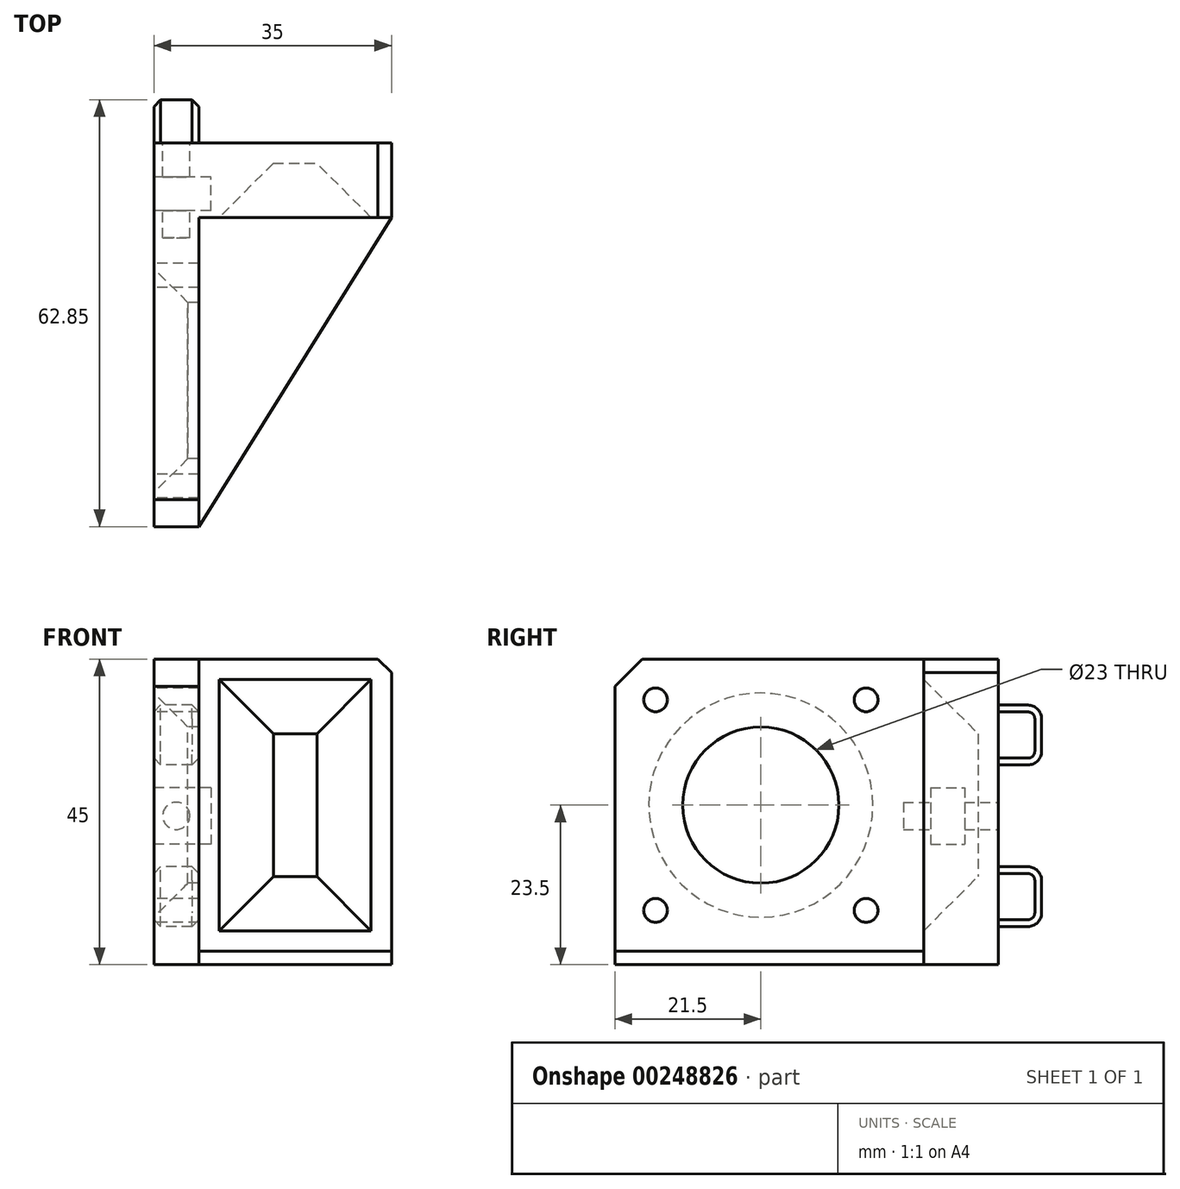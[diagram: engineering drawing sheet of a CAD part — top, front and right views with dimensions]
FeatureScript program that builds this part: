
annotation { "Feature Type Name" : "Feature", "Feature Type Description" : "" }
export const myFeature = defineFeature(function(context is Context, id is Id, definition is map)
    precondition{}
    {
        {
            var Q0;
            Q0=qCreatedBy(makeId("Right.planeOp"),FACE);
            var sketch = newSketch(context, id + "F0", { "sketchPlane" : qUnion([Q0])});
            skCircle(sketch, "E0", {"center": v(0, 0) * mm, "radius": 11.5 * mm});
            skCircle(sketch, "E1", {"center": v(15.5, 15.5) * mm, "radius": 1.75 * mm});
            skCircle(sketch, "E2.MirrorC", {"center": v(-15.5, 15.5) * mm, "radius": 1.75 * mm});
            skCircle(sketch, "E3.MirrorC", {"center": v(-15.5, -15.5) * mm, "radius": 1.75 * mm});
            skCircle(sketch, "E4.MirrorC", {"center": v(15.5, -15.5) * mm, "radius": 1.75 * mm});
            skLineSegment(sketch, "E5", {"start": v(-21.5, 21.5) * mm, "end": v(-21.5, -23.5) * mm});
            skPoint(sketch, "E6", {"position": v(-21.5, -1) * mm});
            skLineSegment(sketch, "E7", {"start": v(-21.5, 21.5) * mm, "end": v(35, 21.5) * mm});
            skLineSegment(sketch, "E8", {"start": v(35, 21.5) * mm, "end": v(35, -23.5) * mm});
            skLineSegment(sketch, "E9", {"start": v(35, -23.5) * mm, "end": v(-21.5, -23.5) * mm});
            skLineSegment(sketch, "E10", {"start": v(24, 21.5) * mm, "end": v(24, -23.5) * mm});
            skLineSegment(sketch, "E11", {"start": v(35, 14.72) * mm, "end": v(41.35, 14.72) * mm});
            skLineSegment(sketch, "E12", {"start": v(41.35, 14.72) * mm, "end": v(41.35, 5.92) * mm});
            skLineSegment(sketch, "E13", {"start": v(41.35, 5.92) * mm, "end": v(35, 5.92) * mm});
            skLineSegment(sketch, "E14", {"start": v(35, -9.08) * mm, "end": v(41.35, -9.08) * mm});
            skLineSegment(sketch, "E15", {"start": v(41.35, -9.08) * mm, "end": v(41.35, -17.88) * mm});
            skLineSegment(sketch, "E16", {"start": v(41.35, -17.88) * mm, "end": v(35, -17.88) * mm});
            skLineSegment(sketch, "E17", {"start": v(-21.5, -21.5) * mm, "end": v(24, -21.5) * mm});
            skSolve(sketch);
        }
        {
            var Q0;
            {var subQ6=sQuery(id+"F0.wireOp",EDGE,"E10");Q0=makeQuery(id+"F0.imprint","IMPRINT",FACE,{"disambiguationData":[TD([[makeQuery(id+"F0.imprint","IMPRINT",EDGE,{"derivedFrom":subQ6}),1.0]])]});}
            var Q1;
            {var subQ3=sQuery(id+"F0.wireOp",EDGE,"E17");Q1=makeQuery(id+"F0.imprint","IMPRINT",FACE,{"disambiguationData":[TD([[makeQuery(id+"F0.imprint","IMPRINT",EDGE,{"derivedFrom":subQ3}),-1.0]])]});}
            extrude(context, id + "F1", {"entities" : qUnion([Q0, Q1]), "depth" : 35 * mm, "offsetDistance" : 25 * mm});
        }
        {
            var Q0;
            Q0=makeQuery(id+"F0.imprint","IMPRINT",FACE,{"disambiguationData":[TD([[makeQuery(id+"F0.imprint","IMPRINT",EDGE,{"derivedFrom":sQuery(id+"F0.wireOp",EDGE,"E0")}),-1.0]])]});
            extrude(context, id + "F2", {"entities" : qUnion([Q0]), "operationType" : NewBodyOperationType.ADD, "depth" : 6.6 * mm, "offsetDistance" : 25 * mm});
        }
        {
            var Q0;
            {var subQ0=sQuery(id+"F0.wireOp",EDGE,"E11");Q0=makeQuery(id+"F0.imprint","IMPRINT",FACE,{"disambiguationData":[TD([[makeQuery(id+"F0.imprint","IMPRINT",EDGE,{"derivedFrom":subQ0}),-1.0]])]});}
            var Q1;
            {var subQ0=sQuery(id+"F0.wireOp",EDGE,"E14");Q1=makeQuery(id+"F0.imprint","IMPRINT",FACE,{"disambiguationData":[TD([[makeQuery(id+"F0.imprint","IMPRINT",EDGE,{"derivedFrom":subQ0}),-1.0]])]});}
            extrude(context, id + "F3", {"entities" : qUnion([Q0, Q1]), "operationType" : NewBodyOperationType.ADD, "depth" : 6.6 * mm, "offsetDistance" : 25 * mm});
        }
        {
            var Q0;
            Q0=makeQuery(id+"F1.opExtrude","SWEPT_FACE",FACE,{"disambiguationData":[OSD([sQuery(id+"F0.wireOp",EDGE,"E8")])]});
            var sketch = newSketch(context, id + "F4", { "sketchPlane" : qUnion([Q0])});
            skLineSegment(sketch, "E18", {"start": v(0, 5.92) * mm, "end": v(0, -9.08) * mm});
            skPoint(sketch, "E19", {"position": v(0, -1.58) * mm});
            skPoint(sketch, "E20", {"position": v(-3.3, -1.58) * mm});
            skPoint(sketch, "E20.positionSnap0", {"position": v(-3.3, -9.08) * mm});
            skCircle(sketch, "E21", {"center": v(-3.3, -1.58) * mm, "radius": 2 * mm});
            skSolve(sketch);
        }
        {
            var Q0;
            Q0=makeQuery(id+"F4.imprint","IMPRINT",FACE,{"disambiguationData":[TD([[makeQuery(id+"F4.imprint","IMPRINT",EDGE,{"derivedFrom":sQuery(id+"F4.wireOp",EDGE,"E21")}),1.0]])]});
            extrude(context, id + "F5", {"entities" : qUnion([Q0]), "operationType" : NewBodyOperationType.REMOVE, "oppositeDirection" : true, "depth" : 14 * mm, "offsetDistance" : 25 * mm});
        }
        {
            var Q0;
            {var subQ0=sQuery(id+"F0.wireOp",EDGE,"E8");var subQ1=sQuery(id+"F0.wireOp",EDGE,"E10");var subQ2=sQuery(id+"F0.wireOp",EDGE,"E9");var subQ3=sQuery(id+"F0.wireOp",EDGE,"E7");Q0=makeQuery(id+"F3.boolean.opBoolean","MERGE",FACE,{"derivedFrom":[makeQuery(id+"F2.boolean.opBoolean","MERGE",FACE,{"derivedFrom":[makeQuery(id+"F1.opExtrude","CAP_FACE",FACE,{"disambiguationData":[OSD([subQ3,subQ0,subQ2,subQ1])],"isStart":true}),makeQuery(id+"F2.opExtrude","CAP_FACE",FACE,{"disambiguationData":[OSD([sQuery(id+"F0.wireOp",EDGE,"E0"),sQuery(id+"F0.wireOp",EDGE,"E1"),sQuery(id+"F0.wireOp",EDGE,"E2.MirrorC"),sQuery(id+"F0.wireOp",EDGE,"E3.MirrorC"),sQuery(id+"F0.wireOp",EDGE,"E4.MirrorC"),sQuery(id+"F0.wireOp",EDGE,"E5"),subQ3,subQ2,subQ1])],"isStart":true})]}),makeQuery(id+"F3.opExtrude","CAP_FACE",FACE,{"disambiguationData":[OSD([subQ0,sQuery(id+"F0.wireOp",EDGE,"E11"),sQuery(id+"F0.wireOp",EDGE,"E12"),sQuery(id+"F0.wireOp",EDGE,"E13")])],"isStart":true}),makeQuery(id+"F3.opExtrude","CAP_FACE",FACE,{"disambiguationData":[OSD([subQ0,sQuery(id+"F0.wireOp",EDGE,"E14"),sQuery(id+"F0.wireOp",EDGE,"E15"),sQuery(id+"F0.wireOp",EDGE,"E16")])],"isStart":true})]});}
            var sketch = newSketch(context, id + "F6", { "sketchPlane" : qUnion([Q0])});
            skLineSegment(sketch, "E22.bottom", {"start": v(-25, 2.57) * mm, "end": v(-30, 2.57) * mm});
            skLineSegment(sketch, "E22.top", {"start": v(-25, -5.73) * mm, "end": v(-30, -5.73) * mm});
            skLineSegment(sketch, "E22.left", {"start": v(-25, 2.57) * mm, "end": v(-25, -5.73) * mm});
            skLineSegment(sketch, "E22.right", {"start": v(-30, 2.57) * mm, "end": v(-30, -5.73) * mm});
            skPoint(sketch, "E22.middle", {"position": v(-27.5, -1.58) * mm});
            skPoint(sketch, "E22.middle.positionSnap0", {"position": v(-35, -1.58) * mm});
            skPoint(sketch, "E22.centerSnap0", {"position": v(-35, -1.58) * mm});
            skSolve(sketch);
        }
        {
            var Q0;
            Q0=makeQuery(id+"F6.imprint","IMPRINT",FACE,{"disambiguationData":[TD([[makeQuery(id+"F6.imprint","IMPRINT",EDGE,{"derivedFrom":sQuery(id+"F6.wireOp",EDGE,"E22.bottom")}),1.0]])]});
            extrude(context, id + "F7", {"entities" : qUnion([Q0]), "operationType" : NewBodyOperationType.REMOVE, "oppositeDirection" : true, "depth" : (0.3 + 3.3 + 9.58 / 2) * mm, "offsetDistance" : 25 * mm});
        }
        {
            var Q0;
            Q0=makeQuery(id+"F1.opExtrude","CAP_EDGE",EDGE,{"disambiguationData":[OSD([sQuery(id+"F0.wireOp",EDGE,"E5")])],"isStart":false});
            chamfer(context, id + "F8", {"entities" : qUnion([Q0]), "chamferType" : ChamferType.TWO_OFFSETS, "width1" : 45.5 * mm, "oppositeDirection" : false, "width2" : 28.4 * mm, "tangentPropagation" : true});
        }
        {
            var Q0;
            Q0=makeQuery(id+"F3.opExtrude","SWEPT_EDGE",EDGE,{"disambiguationData":[OSD([sQuery(id+"F0.wireOp",EDGE,"E11"),sQuery(id+"F0.wireOp",EDGE,"E12")])]});
            var Q1;
            Q1=makeQuery(id+"F3.opExtrude","SWEPT_EDGE",EDGE,{"disambiguationData":[OSD([sQuery(id+"F0.wireOp",EDGE,"E12"),sQuery(id+"F0.wireOp",EDGE,"E13")])]});
            var Q2;
            Q2=makeQuery(id+"F3.opExtrude","SWEPT_EDGE",EDGE,{"disambiguationData":[OSD([sQuery(id+"F0.wireOp",EDGE,"E14"),sQuery(id+"F0.wireOp",EDGE,"E15")])]});
            var Q3;
            Q3=makeQuery(id+"F3.opExtrude","SWEPT_EDGE",EDGE,{"disambiguationData":[OSD([sQuery(id+"F0.wireOp",EDGE,"E15"),sQuery(id+"F0.wireOp",EDGE,"E16")])]});
            fillet(context, id + "F9", {"entities" : qUnion([Q0, Q1, Q2, Q3]), "radius" : 2 * mm, "tangentPropagation" : true, "allowEdgeOverflow" : false});
        }
        {
            var Q0;
            Q0=makeQuery(id+"F3.opExtrude","CAP_EDGE",EDGE,{"disambiguationData":[OSD([sQuery(id+"F0.wireOp",EDGE,"E14")])],"isStart":true});
            var Q1;
            Q1=makeQuery(id+"F3.opExtrude","CAP_EDGE",EDGE,{"disambiguationData":[OSD([sQuery(id+"F0.wireOp",EDGE,"E11")])],"isStart":true});
            var Q2;
            Q2=makeQuery(id+"F3.opExtrude","CAP_EDGE",EDGE,{"disambiguationData":[OSD([sQuery(id+"F0.wireOp",EDGE,"E16")])],"isStart":false});
            var Q3;
            Q3=makeQuery(id+"F3.opExtrude","CAP_EDGE",EDGE,{"disambiguationData":[OSD([sQuery(id+"F0.wireOp",EDGE,"E13")])],"isStart":false});
            chamfer(context, id + "F10", {"entities" : qUnion([Q0, Q1, Q2, Q3]), "width" : 1 * mm, "tangentPropagation" : true});
        }
        {
            var Q0;
            Q0=makeQuery(id+"F2.opExtrude","SWEPT_EDGE",EDGE,{"disambiguationData":[OSD([sQuery(id+"F0.wireOp",EDGE,"E5"),sQuery(id+"F0.wireOp",EDGE,"E7")])]});
            chamfer(context, id + "F11", {"entities" : qUnion([Q0]), "width" : 4 * mm, "tangentPropagation" : true});
        }
        {
            var Q0;
            Q0=makeQuery(id+"F2.opExtrude","CAP_EDGE",EDGE,{"disambiguationData":[OSD([sQuery(id+"F0.wireOp",EDGE,"E0")])],"isStart":true});
            chamfer(context, id + "F12", {"entities" : qUnion([Q0]), "width" : 5 * mm, "tangentPropagation" : true});
        }
        {
            var Q0;
            Q0=makeQuery(id+"F1.opExtrude","SWEPT_FACE",FACE,{"disambiguationData":[OSD([sQuery(id+"F0.wireOp",EDGE,"E10")])]});
            var sketch = newSketch(context, id + "F13", { "sketchPlane" : qUnion([Q0])});
            skLineSegment(sketch, "E23", {"start": v(6.6, 18.5) * mm, "end": v(32, 18.5) * mm});
            skLineSegment(sketch, "E24.MirrorCS", {"start": v(6.6, -18.5) * mm, "end": v(32, -18.5) * mm});
            skLineSegment(sketch, "E25", {"start": v(32, 18.5) * mm, "end": v(32, -18.5) * mm});
            skLineSegment(sketch, "E26", {"start": v(9.6, 18.5) * mm, "end": v(9.6, -18.5) * mm});
            skSolve(sketch);
        }
        {
            var Q0;
            {var subQ0=sQuery(id+"F13.wireOp",EDGE,"E25");Q0=makeQuery(id+"F13.imprint","IMPRINT",FACE,{"disambiguationData":[TD([[makeQuery(id+"F13.imprint","IMPRINT",EDGE,{"derivedFrom":subQ0}),-1.0]])]});}
            extrude(context, id + "F14", {"entities" : qUnion([Q0]), "operationType" : NewBodyOperationType.REMOVE, "oppositeDirection" : true, "depth" : 8 * mm, "offsetDistance" : 25 * mm});
        }
        {
            var Q0;
            Q0=makeQuery(id+"F14.boolean.opBoolean","COPY",FACE,{"derivedFrom":makeQuery(id+"F14.opExtrude","CAP_FACE",FACE,{"disambiguationData":[OSD([sQuery(id+"F13.wireOp",EDGE,"E23"),sQuery(id+"F13.wireOp",EDGE,"E24.MirrorCS"),sQuery(id+"F13.wireOp",EDGE,"E25"),sQuery(id+"F13.wireOp",EDGE,"E26")])],"isStart":false})});
            chamfer(context, id + "F15", {"entities" : qUnion([Q0]), "width" : 8 * mm, "tangentPropagation" : true});
        }
        {
            var Q0;
            Q0=makeQuery(id+"F1.opExtrude","CAP_EDGE",EDGE,{"disambiguationData":[OSD([sQuery(id+"F0.wireOp",EDGE,"E7")])],"isStart":false});
            chamfer(context, id + "F16", {"entities" : qUnion([Q0]), "width" : 2 * mm, "tangentPropagation" : true});
        }
    });
